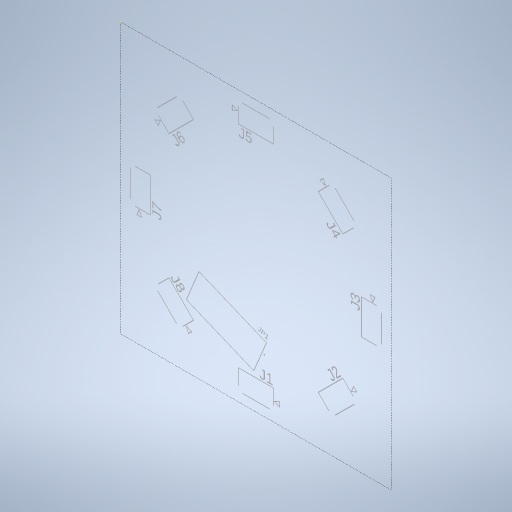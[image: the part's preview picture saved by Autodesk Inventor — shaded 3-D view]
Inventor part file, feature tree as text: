
AUTODESK INVENTOR PART (.ipt)
format: ipt  version: 2024.2 (Build 282272000, 272)  size: 475,136 bytes
history: native  units: in
note: dims shown in document units (in); Inventor stores cm internally (conversion verified against a paired STEP export)
features: sketch x3, extrude x2, other x2
ambient origin geometry x8: Origin, YZ Plane, XZ Plane, XY Plane, X Axis, Y Axis, Z Axis, Center Point
bodies: Solid1 (feature_tree)
feature tree (7):
  sketch  "Sketch1"  dims[d5=2.96in d9=0.01in d10=0.0in]
  extrude  "Extrusion1"  Depth=0.01in TaperAngle=0.0deg
  extrude  "Extrusion2"  TaperAngle=135.0deg  [1 undecoded]
  sketch  "Sketch3"  dims[d15=135.0deg d16=135.0deg d18=1.0in d19=0.0in]
  other  "Image1"
  sketch  "Sketch2"  dims[d13=135.0deg d14=135.0deg]
  other  "Image2"
note: 1 required parameter value undecoded (feature->parameter linkage not recoverable at this tier; creation-order binding heuristic only, values carry confidence <= 0.55)
